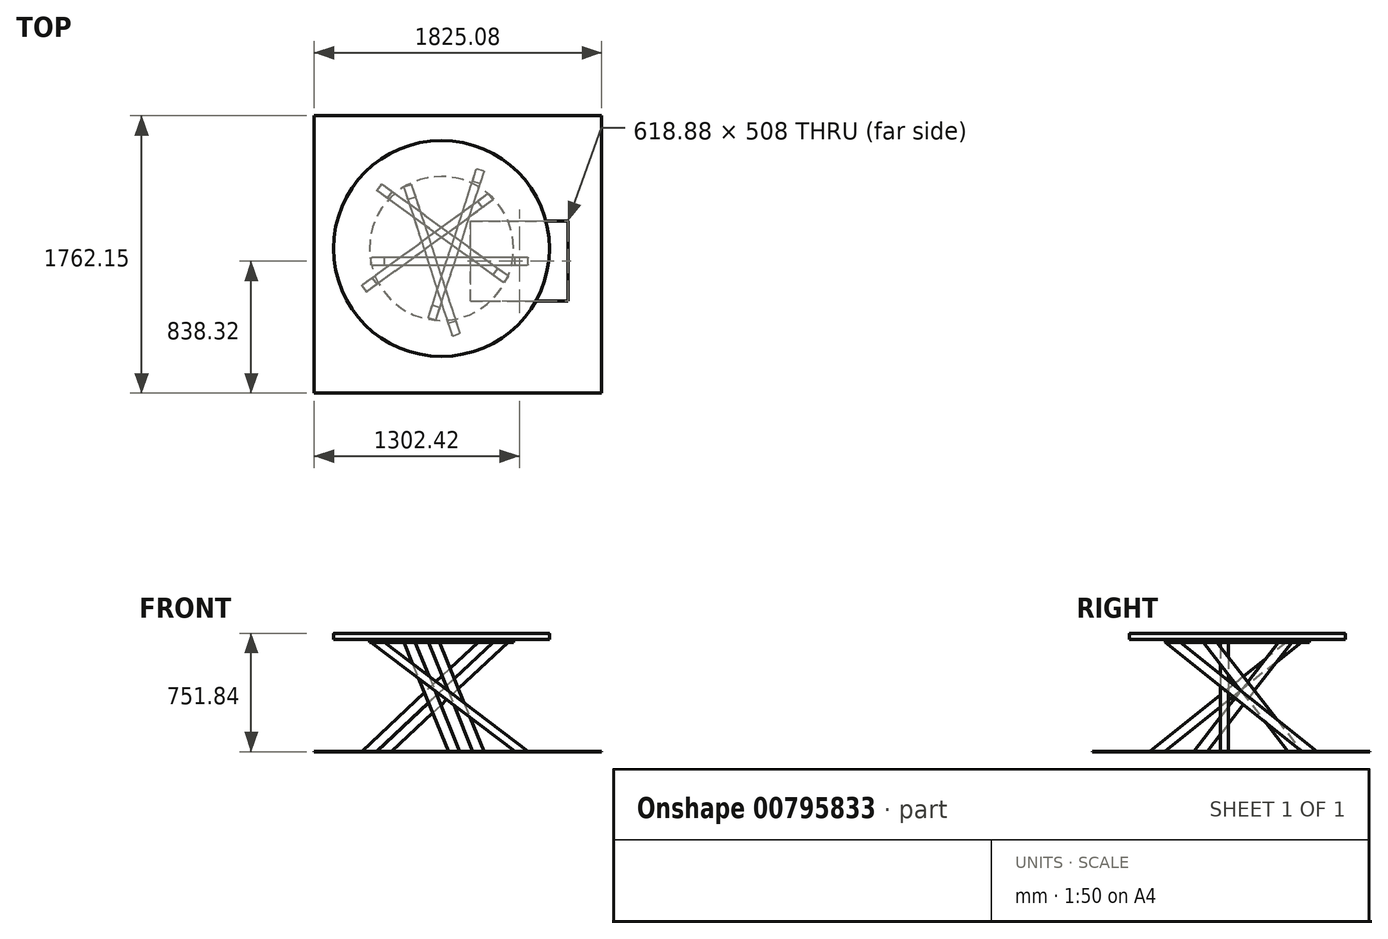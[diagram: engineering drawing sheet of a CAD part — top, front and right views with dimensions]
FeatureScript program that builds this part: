
annotation { "Feature Type Name" : "Feature", "Feature Type Description" : "" }
export const myFeature = defineFeature(function(context is Context, id is Id, definition is map)
    precondition{}
    {
        {
            var Q0;
            Q0=qCreatedBy(makeId("Top.planeOp"),FACE);
            cPlane(context, id + "F0", {"entities" : qUnion([Q0]), "cplaneType" : CPlaneType.OFFSET, "offset" : 749.3 * mm, "width" : 152.4 * mm, "height" : 152.4 * mm});
        }
        {
            var Q0;
            Q0=qCreatedBy(id+"F0.planeOp",FACE);
            var sketch = newSketch(context, id + "F1", { "sketchPlane" : qUnion([Q0])});
            skCircle(sketch, "E0", {"center": v(0, 0) * mm, "radius": 685.8 * mm});
            skSolve(sketch);
        }
        {
            var Q0;
            Q0 = qSketchRegion(id + "F1", true);
            extrude(context, id + "F2", {"entities" : qUnion([Q0]), "oppositeDirection" : true, "depth" : 38.1 * mm, "offsetDistance" : 25.4 * mm});
        }
        {
            var Q0;
            Q0=qCreatedBy(makeId("Top.planeOp"),FACE);
            var sketch = newSketch(context, id + "F3", { "sketchPlane" : qUnion([Q0])});
            skLineSegment(sketch, "E1.bottom", {"start": v(1017.13, -919.6) * mm, "end": v(-807.95, -919.6) * mm});
            skLineSegment(sketch, "E1.top", {"start": v(1017.13, 842.55) * mm, "end": v(-807.95, 842.55) * mm});
            skLineSegment(sketch, "E1.left", {"start": v(1017.13, -919.6) * mm, "end": v(1017.13, 842.55) * mm});
            skLineSegment(sketch, "E1.right", {"start": v(-807.95, -919.6) * mm, "end": v(-807.95, 842.55) * mm});
            skSolve(sketch);
        }
        {
            var Q0;
            Q0=makeQuery(id+"F2.opExtrude","CAP_FACE",FACE,{"disambiguationData":[OSD([sQuery(id+"F1.wireOp",EDGE,"E0")])],"isStart":false});
            var sketch = newSketch(context, id + "F4", { "sketchPlane" : qUnion([Q0])});
            skCircle(sketch, "E2", {"center": v(0, 0) * mm, "radius": 457.2 * mm});
            skSolve(sketch);
        }
        {
            var Q0;
            Q0 = qSketchRegion(id + "F3", true);
            extrude(context, id + "F5", {"entities" : qUnion([Q0]), "oppositeDirection" : true, "depth" : 2.54 * mm, "offsetDistance" : 25.4 * mm});
        }
        {
            var Q0;
            Q0 = qSketchRegion(id + "F4", true);
            extrude(context, id + "F6", {"entities" : qUnion([Q0]), "operationType" : NewBodyOperationType.ADD, "depth" : 19.05 * mm, "offsetDistance" : 25.4 * mm});
        }
        {
            var Q0;
            Q0=makeQuery(id+"F2.opExtrude","CAP_EDGE",EDGE,{"disambiguationData":[OSD([sQuery(id+"F1.wireOp",EDGE,"E0")])],"isStart":true});
            fillet(context, id + "F7", {"entities" : qUnion([Q0]), "radius" : 5.08 * mm, "tangentPropagation" : true, "allowEdgeOverflow" : false});
        }
        {
            var Q0;
            Q0=qCreatedBy(makeId("Front.planeOp"),FACE);
            cPlane(context, id + "F8", {"entities" : qUnion([Q0]), "cplaneType" : CPlaneType.OFFSET, "offset" : 81.28 * mm, "width" : 152.4 * mm, "height" : 152.4 * mm});
        }
        {
            var Q0;
            Q0=qCreatedBy(id+"F8.planeOp",FACE);
            var sketch = newSketch(context, id + "F9", { "sketchPlane" : qUnion([Q0])});
            skLineSegment(sketch, "E3", {"start": v(-612.54, 0) * mm, "end": v(750.3, 0) * mm, "construction": true});
            skLineSegment(sketch, "E4", {"start": v(0, 0) * mm, "end": v(0, 692.15) * mm, "construction": true});
            skLineSegment(sketch, "E5", {"start": v(-613.75, 692.15) * mm, "end": v(649.28, 692.15) * mm, "construction": true});
            skLineSegment(sketch, "E6", {"start": v(-403.86, 692.15) * mm, "end": v(508, 0) * mm});
            skSolve(sketch);
        }
        {
            var Q0;
            Q0=sQuery(id+"F9.wireOp",EDGE,"E6");
            var Q1;
            Q1=sQuery(id+"F9.wireOp",VERTEX,"E6.end");
            cPlane(context, id + "F10", {"entities" : qUnion([Q0, Q1]), "cplaneType" : CPlaneType.LINE_POINT, "offset" : 25.4 * mm, "width" : 152.4 * mm, "height" : 152.4 * mm});
        }
        {
            var Q0;
            Q0=qCreatedBy(id+"F10.planeOp",FACE);
            var sketch = newSketch(context, id + "F11", { "sketchPlane" : qUnion([Q0])});
            skLineSegment(sketch, "E7.bottom", {"start": v(-59.69, 332.54) * mm, "end": v(-102.87, 332.54) * mm});
            skLineSegment(sketch, "E7.top", {"start": v(-59.7, 281.74) * mm, "end": v(-102.87, 281.74) * mm});
            skLineSegment(sketch, "E7.left", {"start": v(-55.88, 328.73) * mm, "end": v(-55.88, 285.55) * mm});
            skLineSegment(sketch, "E7.right", {"start": v(-106.68, 328.73) * mm, "end": v(-106.68, 285.55) * mm});
            skPoint(sketch, "E7.middle", {"position": v(-81.28, 307.14) * mm});
            skPoint(sketch, "E8.visualSharp", {"position": v(-106.68, 332.54) * mm});
            skArc(sketch, "E8.filletArc", {"start": v(-102.87, 332.54) * mm, "mid": v(-105.56, 331.42) * mm, "end": v(-106.68, 328.73) * mm});
            skPoint(sketch, "E9.visualSharp", {"position": v(-55.88, 332.54) * mm});
            skArc(sketch, "E9.filletArc", {"start": v(-55.88, 328.73) * mm, "mid": v(-57, 331.42) * mm, "end": v(-59.69, 332.54) * mm});
            skPoint(sketch, "E10.visualSharp", {"position": v(-55.88, 281.74) * mm});
            skArc(sketch, "E10.filletArc", {"start": v(-59.7, 281.74) * mm, "mid": v(-57, 282.86) * mm, "end": v(-55.88, 285.55) * mm});
            skPoint(sketch, "E11.visualSharp", {"position": v(-106.68, 281.74) * mm});
            skArc(sketch, "E11.filletArc", {"start": v(-106.68, 285.55) * mm, "mid": v(-105.56, 282.86) * mm, "end": v(-102.87, 281.74) * mm});
            skSolve(sketch);
        }
        {
            var Q0;
            Q0 = qSketchRegion(id + "F11", true);
            var Q1;
            Q1=makeQuery(id+"F6.opExtrude","CAP_FACE",FACE,{"disambiguationData":[OSD([sQuery(id+"F4.wireOp",EDGE,"E2")])],"isStart":false});
            extrude(context, id + "F12", {"entities" : qUnion([Q0]), "endBound" : BoundingType.UP_TO_SURFACE, "oppositeDirection" : true, "depth" : 25.4 * mm, "endBoundEntityFace" : qUnion([Q1]), "offsetDistance" : 25.4 * mm, "hasSecondDirection" : true, "secondDirectionOppositeDirection" : false, "secondDirectionDepth" : 127 * mm});
        }
        {
            var Q0;
            Q0=qCreatedBy(id+"F8.planeOp",FACE);
            var sketch = newSketch(context, id + "F13", { "sketchPlane" : qUnion([Q0])});
            skLineSegment(sketch, "E12.bottom", {"start": v(185.03, -277.65) * mm, "end": v(803.92, -277.65) * mm});
            skLineSegment(sketch, "E12.top", {"start": v(185.03, 0) * mm, "end": v(803.92, 0) * mm});
            skLineSegment(sketch, "E12.left", {"start": v(185.03, -277.65) * mm, "end": v(185.03, 0) * mm});
            skLineSegment(sketch, "E12.right", {"start": v(803.92, -277.65) * mm, "end": v(803.92, 0) * mm});
            skSolve(sketch);
        }
        {
            var Q0;
            Q0 = qSketchRegion(id + "F13", true);
            extrude(context, id + "F14", {"entities" : qUnion([Q0]), "operationType" : NewBodyOperationType.REMOVE, "oppositeDirection" : true, "depth" : 254 * mm, "offsetDistance" : 25.4 * mm, "hasSecondDirection" : true, "secondDirectionOppositeDirection" : false, "secondDirectionDepth" : 254 * mm});
        }
        {
            var Q0;
            Q0=qCreatedBy(makeId("Front.planeOp"),FACE);
            var sketch = newSketch(context, id + "F15", { "sketchPlane" : qUnion([Q0])});
            skLineSegment(sketch, "E13.0", {"start": v(0, 0) * mm, "end": v(0, 692.15) * mm, "construction": true});
            skSolve(sketch);
        }
        {
            var Q0;
            Q0=makeQuery(id+"F12.opExtrude","SWEPT_BODY",BODY,{"disambiguationData":[OSD([sQuery(id+"F11.wireOp",EDGE,"E7.bottom"),sQuery(id+"F11.wireOp",EDGE,"E7.top"),sQuery(id+"F11.wireOp",EDGE,"E7.left"),sQuery(id+"F11.wireOp",EDGE,"E7.right"),sQuery(id+"F11.wireOp",EDGE,"E8.filletArc"),sQuery(id+"F11.wireOp",EDGE,"E9.filletArc"),sQuery(id+"F11.wireOp",EDGE,"E10.filletArc"),sQuery(id+"F11.wireOp",EDGE,"E11.filletArc")])]});
            var Q1;
            Q1=sQuery(id+"F15.wireOp",EDGE,"E13.0");
            circularPattern(context, id + "F16", {"entities" : qUnion([Q0]), "axis" : qUnion([Q1]), "angle" : 360 * degree, "instanceCount" : 5, "equalSpace" : true});
        }
    });
